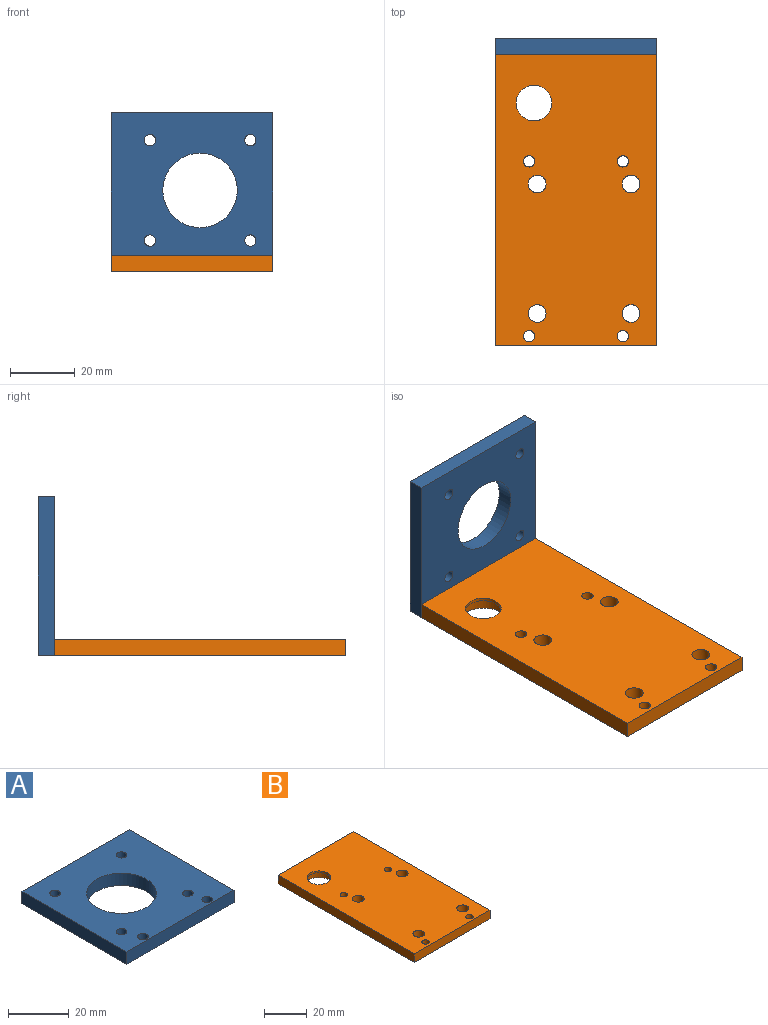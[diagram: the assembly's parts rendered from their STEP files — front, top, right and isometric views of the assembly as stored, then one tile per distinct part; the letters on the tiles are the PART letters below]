
ASSEMBLY  parts=2 mates=1
PART A: 13 faces, bbox 50x49x5 mm
  f0: plane 50x5mm, normal (0,-1,0), area 250mm2, adj f1,f3,f4,f5
  f1: plane 49x5mm, normal (1,0,0), area 245mm2, adj f0,f2,f4,f5
  f2: plane 50x5mm, normal (0,1,0), area 250mm2, adj f1,f3,f4,f5
  f3: plane 49x5mm, normal (-1,0,0), area 245mm2, adj f0,f2,f4,f5
  f4: plane 50x49mm, normal (0,0,1), area 1976.8mm2, adj f0,f1,f2,f3,f6,f7,f8,f9
  f5: plane 50x49mm, normal (0,0,-1), area 1976.8mm2, adj f0,f1,f2,f3,f6,f7,f8,f9
  f6: cylinder r=1.75mm len=5mm, axis (0,0,1), area 55mm2, adj f4,f5
  f7: cylinder r=1.75mm len=5mm, axis (0,0,1), area 55mm2, adj f4,f5
  f8: cylinder r=1.75mm len=5mm, axis (0,0,1), area 55mm2, adj f4,f5
  f9: cylinder r=1.75mm len=5mm, axis (0,0,1), area 55mm2, adj f4,f5
  f10: cylinder r=11.5mm len=23mm, axis (0,0,1), area 361.3mm2, adj f4,f5
  f11: cylinder r=1.75mm len=5mm, axis (0,0,1), area 55mm2, adj f4,f5
  f12: cylinder r=1.75mm len=5mm, axis (0,0,1), area 55mm2, adj f4,f5
PART B: 20 faces, bbox 50x90x5 mm
  f0: cylinder r=7.25mm len=14.5mm, axis (0,0,-1), area 177.1mm2, adj f6,f16,f17
  f1: plane 50x5mm, normal (0,-1,0), area 250mm2, adj f2,f4,f5,f6
  f2: plane 90x5mm, normal (1,0,0), area 450mm2, adj f1,f3,f5,f6
  f3: plane 50x5mm, normal (0,1,0), area 240.2mm2, adj f2,f4,f5,f6,f17,f19
  f4: plane 90x5mm, normal (-1,0,0), area 450mm2, adj f1,f3,f5,f6
  f5: plane 90x50mm, normal (0,0,1), area 4271.4mm2, adj f1,f2,f3,f4,f7,f8,f9,f10
  f6: plane 90x50mm, normal (0,0,-1), area 4201.4mm2, adj f0,f1,f2,f3,f4,f7,f8,f9
  f7: cylinder r=1.75mm len=5mm, axis (0,0,-1), area 55mm2, adj f5,f6
  f8: cylinder r=1.75mm len=5mm, axis (0,0,-1), area 55mm2, adj f5,f6
  f9: cylinder r=1.75mm len=5mm, axis (0,0,-1), area 55mm2, adj f5,f6
  f10: cylinder r=1.75mm len=5mm, axis (0,0,-1), area 55mm2, adj f5,f6
  f11: cylinder r=2.75mm len=5.5mm, axis (0,0,-1), area 86.4mm2, adj f5,f6
  f12: cylinder r=2.75mm len=5.5mm, axis (0,0,-1), area 86.4mm2, adj f5,f6
  f13: cylinder r=2.75mm len=5.5mm, axis (0,0,-1), area 86.4mm2, adj f5,f6
  f14: cylinder r=2.75mm len=5.5mm, axis (0,0,-1), area 86.4mm2, adj f5,f6
  f15: cylinder r=5.5mm len=11mm, axis (0,0,-1), area 34.6mm2, adj f5,f16
  f16: plane 14.5x14.5mm, normal (0,0,-1), area 70.1mm2, adj f0,f15
  f17: cylinder r=1.25mm len=8.52mm, axis (0,1,0), area 63.6mm2, adj f0,f3
  f18: cone r=0mm half-angle=59deg, axis (0,1,0), area 5.7mm2, adj f19
  f19: cylinder r=1.25mm len=10mm, axis (0,1,0), area 78.5mm2, adj f3,f18
PLACE A rot(axis=(0,0.71,0.71),180deg) t=(-0.45,45.7,24.5)mm
PLACE B t=(-0.45,0.7,0)mm
MATE fastened A.f12 <-> B.f18  axis (0,-1,0) through (14.55,45.7,2.5)mm
